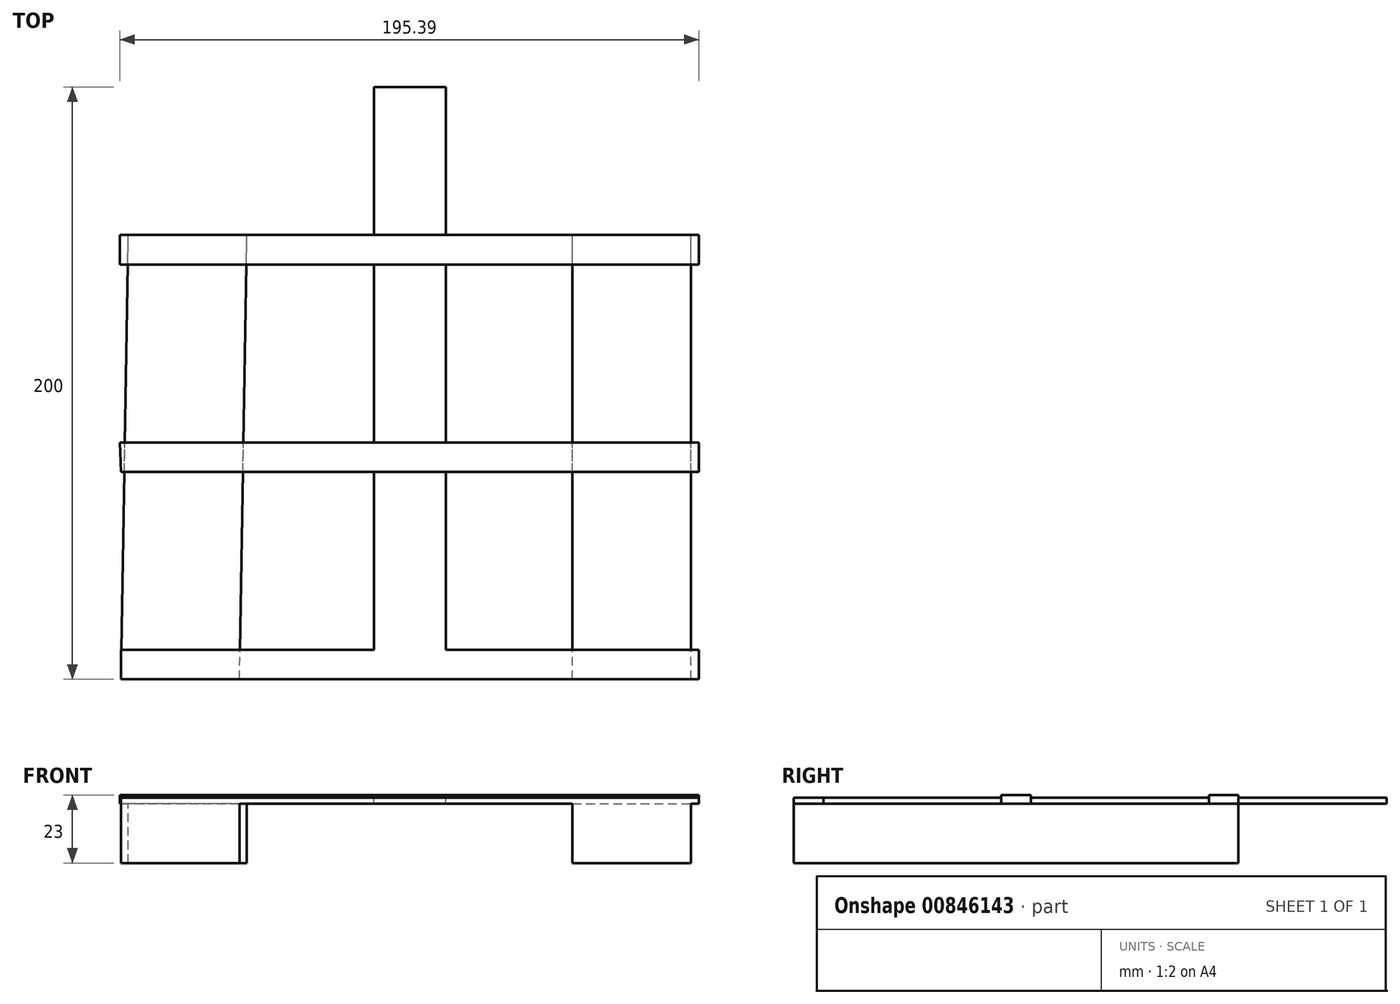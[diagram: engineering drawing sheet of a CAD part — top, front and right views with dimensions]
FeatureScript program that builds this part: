
annotation { "Feature Type Name" : "Feature", "Feature Type Description" : "" }
export const myFeature = defineFeature(function(context is Context, id is Id, definition is map)
    precondition{}
    {
        {
            var Q0;
            Q0=qCreatedBy(makeId("Top.planeOp"),FACE);
            var sketch = newSketch(context, id + "F0", { "sketchPlane" : qUnion([Q0])});
            skLineSegment(sketch, "E0", {"start": v(0, 0) * mm, "end": v(12.13, 0) * mm});
            skLineSegment(sketch, "E1", {"start": v(12.13, 0) * mm, "end": v(-12.13, 0) * mm});
            skLineSegment(sketch, "E2", {"start": v(-12.13, 0) * mm, "end": v(-12.13, 200) * mm});
            skLineSegment(sketch, "E3", {"start": v(12.13, 0) * mm, "end": v(12.13, 200) * mm});
            skLineSegment(sketch, "E4", {"start": v(12.13, 200) * mm, "end": v(-12.13, 200) * mm});
            skSolve(sketch);
        }
        {
            var Q0;
            Q0 = qSketchRegion(id + "F0", true);
            extrude(context, id + "F1", {"entities" : qUnion([Q0]), "depth" : 2 * mm, "offsetDistance" : 25 * mm});
        }
        {
            var Q0;
            Q0=qCreatedBy(makeId("Top.planeOp"),FACE);
            var sketch = newSketch(context, id + "F2", { "sketchPlane" : qUnion([Q0])});
            skLineSegment(sketch, "E5", {"start": v(0, 0) * mm, "end": v(-97.5, 0) * mm});
            skLineSegment(sketch, "E6", {"start": v(0, 0) * mm, "end": v(97.5, 0) * mm});
            skLineSegment(sketch, "E7", {"start": v(-97.5, 0) * mm, "end": v(-97.5, 10) * mm});
            skLineSegment(sketch, "E8", {"start": v(97.5, 10) * mm, "end": v(97.5, 0) * mm});
            skLineSegment(sketch, "E9", {"start": v(0, 70) * mm, "end": v(-97.5, 70) * mm});
            skLineSegment(sketch, "E10", {"start": v(0, 70) * mm, "end": v(97.5, 70) * mm});
            skLineSegment(sketch, "E11", {"start": v(97.5, 70) * mm, "end": v(97.5, 80) * mm});
            skLineSegment(sketch, "E12", {"start": v(97.5, 80) * mm, "end": v(-97.89, 80) * mm});
            skLineSegment(sketch, "E13", {"start": v(-97.89, 80) * mm, "end": v(-97.5, 70) * mm});
            skLineSegment(sketch, "E14", {"start": v(0, 140) * mm, "end": v(-97.89, 140) * mm});
            skLineSegment(sketch, "E15", {"start": v(-97.89, 140) * mm, "end": v(-97.89, 150) * mm});
            skLineSegment(sketch, "E16", {"start": v(-97.89, 150) * mm, "end": v(97.5, 150) * mm});
            skLineSegment(sketch, "E17", {"start": v(97.5, 150) * mm, "end": v(97.5, 140) * mm});
            skLineSegment(sketch, "E18", {"start": v(97.5, 140) * mm, "end": v(0, 140) * mm});
            skLineSegment(sketch, "E19", {"start": v(-97.5, 10) * mm, "end": v(97.5, 10) * mm});
            skSolve(sketch);
        }
        {
            var Q0;
            Q0 = qSketchRegion(id + "F2", true);
            extrude(context, id + "F3", {"entities" : qUnion([Q0]), "operationType" : NewBodyOperationType.ADD, "depth" : 2 * mm, "offsetDistance" : 25 * mm});
        }
        {
            var Q0;
            Q0=makeQuery(id+"F2.imprint","IMPRINT",FACE,{"disambiguationData":[TD([[makeQuery(id+"F2.imprint","IMPRINT",EDGE,{"derivedFrom":sQuery(id+"F2.wireOp",EDGE,"E9")}),-1.0]])]});
            var Q1;
            Q1=makeQuery(id+"F2.imprint","IMPRINT",FACE,{"disambiguationData":[TD([[makeQuery(id+"F2.imprint","IMPRINT",EDGE,{"derivedFrom":sQuery(id+"F2.wireOp",EDGE,"E14")}),-1.0]])]});
            extrude(context, id + "F4", {"entities" : qUnion([Q0, Q1]), "operationType" : NewBodyOperationType.ADD, "depth" : 3 * mm, "offsetDistance" : 25 * mm});
        }
        {
            var Q0;
            Q0 = qSketchRegion(id + "F2", true);
            extrude(context, id + "F5", {"entities" : qUnion([Q0]), "operationType" : NewBodyOperationType.ADD, "depth" : 2 * mm, "offsetDistance" : 25 * mm});
        }
        {
            var Q0;
            Q0=makeQuery(id+"F3.boolean.opBoolean","MERGE",FACE,{"derivedFrom":[makeQuery(id+"F1.opExtrude","CAP_FACE",FACE,{"disambiguationData":[OSD([sQuery(id+"F0.wireOp",EDGE,"E1"),sQuery(id+"F0.wireOp",EDGE,"E2"),sQuery(id+"F0.wireOp",EDGE,"E3"),sQuery(id+"F0.wireOp",EDGE,"E4")])],"isStart":true}),makeQuery(id+"F3.opExtrude","CAP_FACE",FACE,{"disambiguationData":[OSD([sQuery(id+"F2.wireOp",EDGE,"E5"),sQuery(id+"F2.wireOp",EDGE,"E6"),sQuery(id+"F2.wireOp",EDGE,"E7"),sQuery(id+"F2.wireOp",EDGE,"E8"),sQuery(id+"F2.wireOp",EDGE,"E19")])],"isStart":true}),makeQuery(id+"F3.opExtrude","CAP_FACE",FACE,{"disambiguationData":[OSD([sQuery(id+"F2.wireOp",EDGE,"E9"),sQuery(id+"F2.wireOp",EDGE,"E10"),sQuery(id+"F2.wireOp",EDGE,"E11"),sQuery(id+"F2.wireOp",EDGE,"E12"),sQuery(id+"F2.wireOp",EDGE,"E13")])],"isStart":true}),makeQuery(id+"F3.opExtrude","CAP_FACE",FACE,{"disambiguationData":[OSD([sQuery(id+"F2.wireOp",EDGE,"E14"),sQuery(id+"F2.wireOp",EDGE,"E15"),sQuery(id+"F2.wireOp",EDGE,"E16"),sQuery(id+"F2.wireOp",EDGE,"E17"),sQuery(id+"F2.wireOp",EDGE,"E18")])],"isStart":true})]});
            var sketch = newSketch(context, id + "F6", { "sketchPlane" : qUnion([Q0])});
            skLineSegment(sketch, "E20.bottom", {"start": v(-97.5, 0) * mm, "end": v(-57.5, 0) * mm});
            skLineSegment(sketch, "E20.top", {"start": v(-95.01, -150) * mm, "end": v(-55, -150) * mm});
            skLineSegment(sketch, "E20.left", {"start": v(-97.5, 0) * mm, "end": v(-95.01, -150) * mm});
            skLineSegment(sketch, "E20.right", {"start": v(-57.5, 0) * mm, "end": v(-55, -150) * mm});
            skLineSegment(sketch, "E21.bottom", {"start": v(97.5, 0) * mm, "end": v(54.82, 0) * mm});
            skLineSegment(sketch, "E21.top", {"start": v(94.82, -150) * mm, "end": v(54.82, -150) * mm});
            skLineSegment(sketch, "E21.left", {"start": v(94.82, 0) * mm, "end": v(94.82, -150) * mm});
            skLineSegment(sketch, "E21.right", {"start": v(54.82, 0) * mm, "end": v(54.82, -150) * mm});
            skSolve(sketch);
        }
        {
            var Q0;
            {var subQ0=sQuery(id+"F6.wireOp",EDGE,"E20.top");Q0=makeQuery(id+"F6.imprint","IMPRINT",FACE,{"disambiguationData":[TD([[makeQuery(id+"F6.imprint","IMPRINT",EDGE,{"derivedFrom":subQ0}),1.0]])]});}
            var Q1;
            {var subQ0=sQuery(id+"F6.wireOp",EDGE,"E20.left");var subQ2=sQuery(id+"F2.wireOp",EDGE,"E12");var subQ5=sQuery(id+"F0.wireOp",EDGE,"E2");var subQ6=makeQuery(id+"F1.opExtrude","SWEPT_FACE",FACE,{"disambiguationData":[OSD([subQ5])]});var subQ12=makeQuery(id+"F3.boolean.opBoolean","SPLIT",EDGE,{"disambiguationData":[TD([subQ6])],"derivedFrom":makeQuery(id+"F3.opExtrude","CAP_EDGE",EDGE,{"disambiguationData":[OSD([subQ2])],"isStart":true})});var subQ13=makeQuery(id+"F6.imprint","INTERSECT",VERTEX,{"derivedFrom":[subQ12,subQ0]});Q1=makeQuery(id+"F6.imprint","IMPRINT",FACE,{"disambiguationData":[TD([[makeQuery(id+"F6.imprint","IMPRINT",EDGE,{"disambiguationData":[TD([[subQ13,-1.0]])],"derivedFrom":subQ0}),1.0]])]});}
            var Q2;
            {var subQ0=sQuery(id+"F6.wireOp",EDGE,"E20.left");var subQ2=sQuery(id+"F2.wireOp",EDGE,"E19");var subQ4=sQuery(id+"F0.wireOp",EDGE,"E2");var subQ5=makeQuery(id+"F1.opExtrude","SWEPT_FACE",FACE,{"disambiguationData":[OSD([subQ4])]});var subQ12=makeQuery(id+"F3.boolean.opBoolean","SPLIT",EDGE,{"disambiguationData":[TD([subQ5])],"derivedFrom":makeQuery(id+"F3.opExtrude","CAP_EDGE",EDGE,{"disambiguationData":[OSD([subQ2])],"isStart":true})});var subQ13=makeQuery(id+"F6.imprint","INTERSECT",VERTEX,{"derivedFrom":[subQ12,subQ0]});Q2=makeQuery(id+"F6.imprint","IMPRINT",FACE,{"disambiguationData":[TD([[makeQuery(id+"F6.imprint","IMPRINT",EDGE,{"disambiguationData":[TD([[subQ13,-1.0]])],"derivedFrom":subQ0}),1.0]])]});}
            var Q3;
            {var subQ0=sQuery(id+"F6.wireOp",EDGE,"E20.bottom");Q3=makeQuery(id+"F6.imprint","IMPRINT",FACE,{"disambiguationData":[TD([[makeQuery(id+"F6.imprint","IMPRINT",EDGE,{"derivedFrom":subQ0}),1.0]])]});}
            var Q4;
            {var subQ1=sQuery(id+"F6.wireOp",EDGE,"E21.bottom");var subQ6=sQuery(id+"F6.wireOp",EDGE,"E21.left");var subQ7=makeQuery(id+"F6.imprint","INTERSECT",VERTEX,{"derivedFrom":[subQ1,subQ6]});Q4=makeQuery(id+"F6.imprint","IMPRINT",FACE,{"disambiguationData":[TD([[makeQuery(id+"F6.imprint","IMPRINT",EDGE,{"disambiguationData":[TD([[subQ7,-1.0]])],"derivedFrom":subQ1}),1.0]])]});}
            var Q5;
            {var subQ0=sQuery(id+"F6.wireOp",EDGE,"E21.left");var subQ2=sQuery(id+"F2.wireOp",EDGE,"E19");var subQ4=sQuery(id+"F0.wireOp",EDGE,"E3");var subQ5=makeQuery(id+"F1.opExtrude","SWEPT_FACE",FACE,{"disambiguationData":[OSD([subQ4])]});var subQ12=makeQuery(id+"F3.boolean.opBoolean","SPLIT",EDGE,{"disambiguationData":[TD([subQ5])],"derivedFrom":makeQuery(id+"F3.opExtrude","CAP_EDGE",EDGE,{"disambiguationData":[OSD([subQ2])],"isStart":true})});var subQ13=makeQuery(id+"F6.imprint","INTERSECT",VERTEX,{"derivedFrom":[subQ12,subQ0]});Q5=makeQuery(id+"F6.imprint","IMPRINT",FACE,{"disambiguationData":[TD([[makeQuery(id+"F6.imprint","IMPRINT",EDGE,{"disambiguationData":[TD([[subQ13,-1.0]])],"derivedFrom":subQ0}),-1.0]])]});}
            var Q6;
            {var subQ0=sQuery(id+"F6.wireOp",EDGE,"E21.left");var subQ1=sQuery(id+"F2.wireOp",EDGE,"E12");var subQ5=sQuery(id+"F0.wireOp",EDGE,"E3");var subQ6=makeQuery(id+"F1.opExtrude","SWEPT_FACE",FACE,{"disambiguationData":[OSD([subQ5])]});var subQ12=makeQuery(id+"F3.boolean.opBoolean","SPLIT",EDGE,{"disambiguationData":[TD([subQ6])],"derivedFrom":makeQuery(id+"F3.opExtrude","CAP_EDGE",EDGE,{"disambiguationData":[OSD([subQ1])],"isStart":true})});var subQ13=makeQuery(id+"F6.imprint","INTERSECT",VERTEX,{"derivedFrom":[subQ12,subQ0]});Q6=makeQuery(id+"F6.imprint","IMPRINT",FACE,{"disambiguationData":[TD([[makeQuery(id+"F6.imprint","IMPRINT",EDGE,{"disambiguationData":[TD([[subQ13,-1.0]])],"derivedFrom":subQ0}),-1.0]])]});}
            var Q7;
            {var subQ0=sQuery(id+"F6.wireOp",EDGE,"E21.left");var subQ4=sQuery(id+"F0.wireOp",EDGE,"E3");var subQ5=makeQuery(id+"F1.opExtrude","SWEPT_FACE",FACE,{"disambiguationData":[OSD([subQ4])]});var subQ7=sQuery(id+"F2.wireOp",EDGE,"E12");var subQ14=makeQuery(id+"F3.boolean.opBoolean","SPLIT",EDGE,{"disambiguationData":[TD([subQ5])],"derivedFrom":makeQuery(id+"F3.opExtrude","CAP_EDGE",EDGE,{"disambiguationData":[OSD([subQ7])],"isStart":true})});var subQ15=makeQuery(id+"F6.imprint","INTERSECT",VERTEX,{"derivedFrom":[subQ14,subQ0]});Q7=makeQuery(id+"F6.imprint","IMPRINT",FACE,{"disambiguationData":[TD([[makeQuery(id+"F6.imprint","IMPRINT",EDGE,{"disambiguationData":[TD([[subQ15,1.0]])],"derivedFrom":subQ0}),-1.0]])]});}
            var Q8;
            {var subQ0=sQuery(id+"F6.wireOp",EDGE,"E21.top");Q8=makeQuery(id+"F6.imprint","IMPRINT",FACE,{"disambiguationData":[TD([[makeQuery(id+"F6.imprint","IMPRINT",EDGE,{"derivedFrom":subQ0}),1.0]])]});}
            var Q9;
            {var subQ0=sQuery(id+"F6.wireOp",EDGE,"E20.left");var subQ4=sQuery(id+"F0.wireOp",EDGE,"E2");var subQ5=makeQuery(id+"F1.opExtrude","SWEPT_FACE",FACE,{"disambiguationData":[OSD([subQ4])]});var subQ8=sQuery(id+"F2.wireOp",EDGE,"E12");var subQ14=makeQuery(id+"F3.boolean.opBoolean","SPLIT",EDGE,{"disambiguationData":[TD([subQ5])],"derivedFrom":makeQuery(id+"F3.opExtrude","CAP_EDGE",EDGE,{"disambiguationData":[OSD([subQ8])],"isStart":true})});var subQ15=makeQuery(id+"F6.imprint","INTERSECT",VERTEX,{"derivedFrom":[subQ14,subQ0]});Q9=makeQuery(id+"F6.imprint","IMPRINT",FACE,{"disambiguationData":[TD([[makeQuery(id+"F6.imprint","IMPRINT",EDGE,{"disambiguationData":[TD([[subQ15,1.0]])],"derivedFrom":subQ0}),1.0]])]});}
            extrude(context, id + "F7", {"entities" : qUnion([Q0, Q1, Q2, Q3, Q4, Q5, Q6, Q7, Q8, Q9]), "operationType" : NewBodyOperationType.ADD, "depth" : 20 * mm, "offsetDistance" : 25 * mm});
        }
    });
